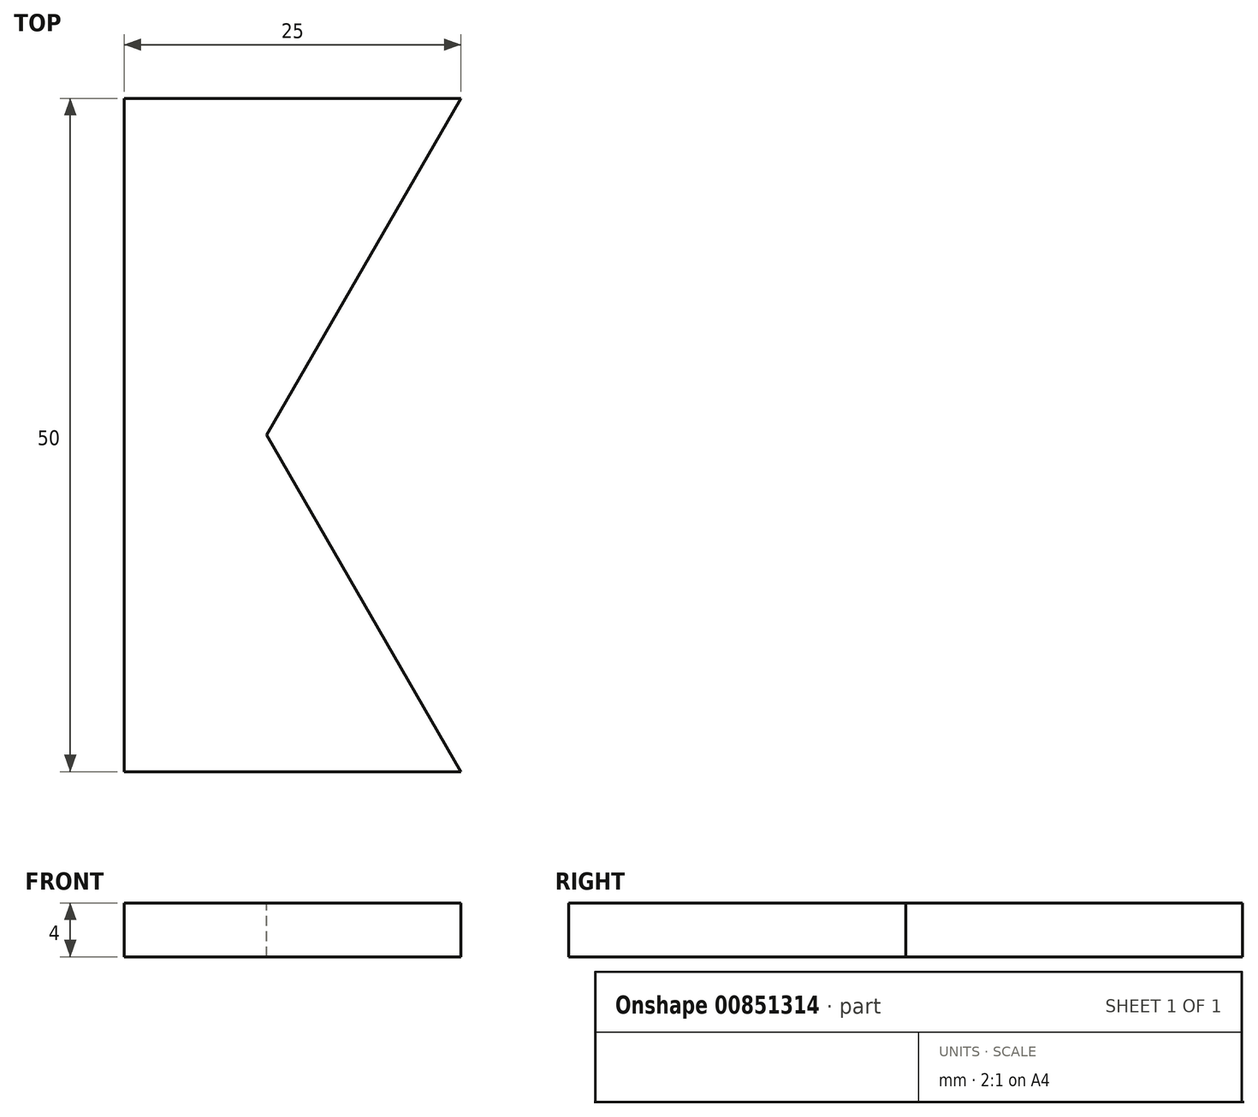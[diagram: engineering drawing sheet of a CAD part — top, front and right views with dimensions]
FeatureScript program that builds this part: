
annotation { "Feature Type Name" : "Feature", "Feature Type Description" : "" }
export const myFeature = defineFeature(function(context is Context, id is Id, definition is map)
    precondition{}
    {
        {
            var Q0;
            Q0=qCreatedBy(makeId("Top.planeOp"),FACE);
            var sketch = newSketch(context, id + "F0", { "sketchPlane" : qUnion([Q0])});
            skLineSegment(sketch, "E0.bottom", {"start": v(0, 0) * mm, "end": v(50, 0) * mm});
            skLineSegment(sketch, "E0.top", {"start": v(0, -50) * mm, "end": v(50, -50) * mm});
            skLineSegment(sketch, "E0.left", {"start": v(0, 0) * mm, "end": v(0, -50) * mm});
            skLineSegment(sketch, "E0.right", {"start": v(50, 0) * mm, "end": v(50, -50) * mm});
            skSolve(sketch);
        }
        {
            var Q0;
            Q0 = qSketchRegion(id + "F0", true);
            extrude(context, id + "F1", {"entities" : qUnion([Q0]), "depth" : 4 * mm, "offsetDistance" : 25 * mm});
        }
        {
            var Q0;
            Q0=makeQuery(id+"F1.opExtrude","CAP_FACE",FACE,{"disambiguationData":[OSD([sQuery(id+"F0.wireOp",EDGE,"E0.bottom"),sQuery(id+"F0.wireOp",EDGE,"E0.top"),sQuery(id+"F0.wireOp",EDGE,"E0.left"),sQuery(id+"F0.wireOp",EDGE,"E0.right")])],"isStart":false});
            var sketch = newSketch(context, id + "F2", { "sketchPlane" : qUnion([Q0])});
            skLineSegment(sketch, "E1", {"start": v(25, 0) * mm, "end": v(10.57, -25) * mm});
            skLineSegment(sketch, "E2", {"start": v(10.57, -25) * mm, "end": v(25, -50) * mm});
            skLineSegment(sketch, "E3", {"start": v(25, -50) * mm, "end": v(50, -50) * mm});
            skLineSegment(sketch, "E4", {"start": v(50, -50) * mm, "end": v(50, 0) * mm});
            skLineSegment(sketch, "E5", {"start": v(50, 0) * mm, "end": v(25, 0) * mm});
            skSolve(sketch);
        }
        {
            var Q0;
            Q0 = qSketchRegion(id + "F2", true);
            extrude(context, id + "F3", {"entities" : qUnion([Q0]), "operationType" : NewBodyOperationType.REMOVE, "endBound" : BoundingType.THROUGH_ALL, "oppositeDirection" : true, "depth" : 25 * mm, "offsetDistance" : 25 * mm});
        }
    });
